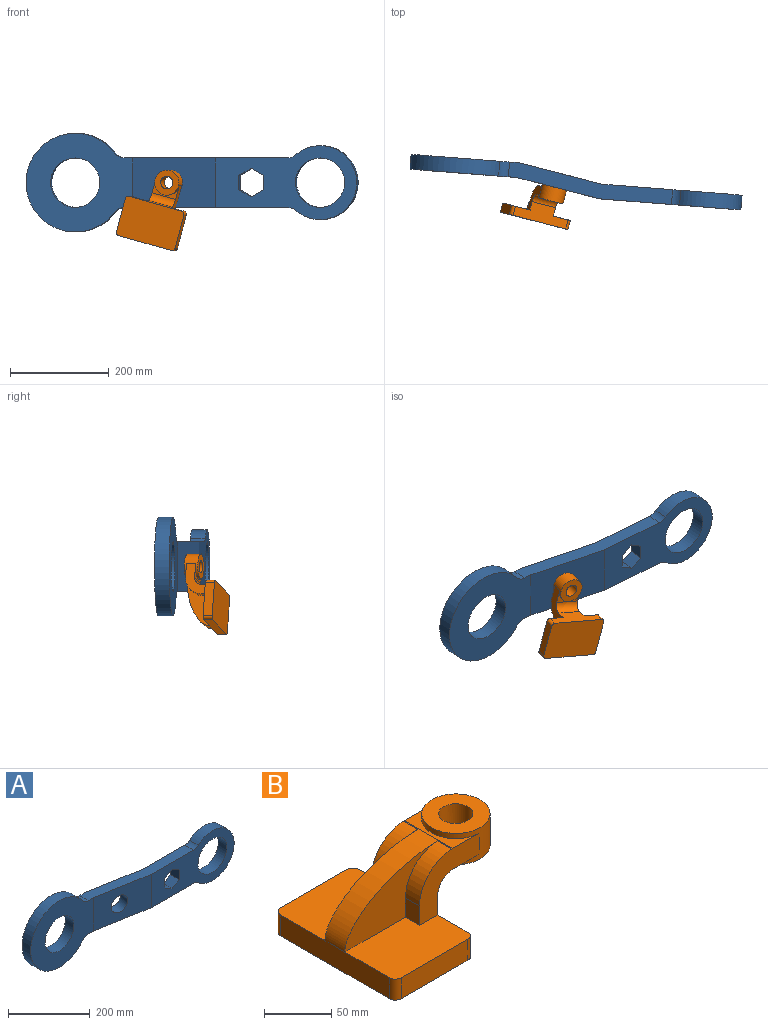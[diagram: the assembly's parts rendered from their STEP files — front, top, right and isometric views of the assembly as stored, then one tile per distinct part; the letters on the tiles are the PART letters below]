
ASSEMBLY  parts=2 mates=1
PART A: 23 faces, bbox 675x60x200 mm
  f0: plane 284.86x150mm, normal (0,1,0), area 21762.9mm2, adj f2,f3,f6,f7,f8,f14,f15,f17
  f1: plane 287.49x150mm, normal (0,-1,0), area 22025.4mm2, adj f2,f4,f6,f7,f8,f14,f15,f17
  f2: cylinder r=50mm len=100mm, axis (0,1,0), area 9424.8mm2, adj f0,f1
  f3: plane 170.14x100mm, normal (0.17,0.98,0), area 15312.8mm2, adj f0,f6,f8,f11,f16
  f4: plane 170.14x100mm, normal (-0.17,-0.98,0), area 15312.8mm2, adj f1,f5,f6,f8,f16
  f5: plane 217.38x200mm, normal (0,-1,0), area 25784.9mm2, adj f4,f6,f8,f9,f10,f12,f13
  f6: plane 333.86x60mm, normal (0,0,-1), area 10094.4mm2, adj f0,f1,f3,f4,f5,f11,f13,f14
  f7: cylinder r=75mm len=150mm, axis (0,1,0), area 10320.9mm2, adj f0,f1,f14,f15
  f8: plane 333.86x60mm, normal (0,0,1), area 10094.4mm2, adj f0,f1,f3,f4,f5,f11,f12,f15
  f9: cylinder r=100mm len=200mm, axis (0,1,0), area 14988.5mm2, adj f5,f11,f12,f13
  f10: cylinder r=50mm len=100mm, axis (0,1,0), area 9424.8mm2, adj f5,f11
  f11: plane 220x200mm, normal (0,1,0), area 26047.4mm2, adj f3,f6,f8,f9,f10,f12,f13
  f12: cylinder r=25mm len=30mm, axis (0,1,0), area 695.5mm2, adj f5,f8,f9,f11
  f13: cylinder r=25mm len=30mm, axis (0,1,0), area 695.5mm2, adj f5,f6,f9,f11
  f14: cylinder r=25mm len=30mm, axis (0,1,0), area 542.1mm2, adj f0,f1,f6,f7
  f15: cylinder r=25mm len=30mm, axis (0,1,0), area 542.1mm2, adj f0,f1,f7,f8
  f16: cylinder r=25mm len=54.45mm, axis (-0.17,-0.98,0), area 4712.4mm2, adj f3,f4
  f17: plane 30x25mm, normal (-0.5,0,-0.87), area 866mm2, adj f0,f1,f18,f22
  f18: plane 30x25mm, normal (0.5,0,-0.87), area 866mm2, adj f0,f1,f17,f19
  f19: plane 30x28.87mm, normal (1,0,0), area 866mm2, adj f0,f1,f18,f20
  f20: plane 30x25mm, normal (0.5,0,0.87), area 866mm2, adj f0,f1,f19,f21
  f21: plane 30x25mm, normal (-0.5,0,0.87), area 866mm2, adj f0,f1,f20,f22
  f22: plane 30x28.87mm, normal (-1,0,0), area 866mm2, adj f0,f1,f17,f21
PART B: 27 faces, bbox 152.4x127x76.2 mm
  f0: plane 17.48x14.92mm, normal (-1,0,0), area 260.8mm2, adj f1,f2,f16,f18
  f1: plane 82.55x53.02mm, normal (0,0,1), area 4075.4mm2, adj f0,f4,f6,f8,f16,f18,f22,f23
  f2: cylinder r=34.92mm len=34.92mm, axis (0,1,0), area 806.4mm2, adj f0,f11,f16,f18
  f3: plane 82.55x53.02mm, normal (0,0,1), area 4075.4mm2, adj f4,f6,f7,f13,f15,f17,f24,f25
  f4: plane 114.3x19.05mm, normal (-1,0,0), area 2177.4mm2, adj f1,f3,f5,f11,f22,f24
  f5: plane 127x82.55mm, normal (0,0,-1), area 10449.2mm2, adj f4,f6,f7,f8,f22,f23,f24,f25
  f6: plane 114.3x36.53mm, normal (1,0,0), area 3065.2mm2, adj f1,f3,f5,f14,f15,f16,f23,f25
  f7: plane 69.85x19.05mm, normal (0,-1,0), area 1330.6mm2, adj f3,f5,f24,f25
  f8: plane 69.85x19.05mm, normal (0,1,0), area 1330.6mm2, adj f1,f5,f22,f23
  f9: plane 50.8x28.58mm, normal (0,0,-1), area 438.2mm2, adj f14,f15,f16,f19
  f10: plane 50.8x28.58mm, normal (0,0,1), area 438.2mm2, adj f11,f15,f16,f19
  f11: extruded ~98.43x52.4mm, area 2524.3mm2, adj f2,f4,f10,f12,f15,f16,f17,f18
  f12: cylinder r=34.92mm len=34.92mm, axis (0,1,0), area 806.4mm2, adj f11,f13,f15,f17
  f13: plane 17.48x14.92mm, normal (-1,0,0), area 260.8mm2, adj f3,f12,f15,f17
  f14: cylinder r=15.88mm len=50.8mm, axis (0,1,0), area 1266.8mm2, adj f6,f9,f15,f16
  f15: plane 63.5x52.4mm, normal (0,-1,0), area 1637.3mm2, adj f3,f6,f9,f10,f11,f12,f13,f14
  f16: plane 63.5x52.4mm, normal (0,1,0), area 1637.3mm2, adj f0,f1,f2,f6,f9,f10,f11,f14
  f17: plane 98.45x52.4mm, normal (0,-1,0), area 2323.5mm2, adj f3,f11,f12,f13
  f18: plane 98.45x52.4mm, normal (0,1,0), area 2323.5mm2, adj f0,f1,f2,f11
  f19: cylinder r=25.4mm len=50.8mm, axis (0,0,-1), area 3040.2mm2, adj f9,f10,f15,f16,f20,f21
  f20: plane 50.8x50.8mm, normal (0,0,-1), area 1520.1mm2, adj f19,f26
  f21: plane 50.8x50.8mm, normal (0,0,1), area 1520.1mm2, adj f19,f26
  f22: cylinder r=6.35mm len=19.05mm, axis (0,0,-1), area 190mm2, adj f1,f4,f5,f8
  f23: cylinder r=6.35mm len=19.05mm, axis (0,0,1), area 190mm2, adj f1,f5,f6,f8
  f24: cylinder r=6.35mm len=19.05mm, axis (0,0,1), area 190mm2, adj f3,f4,f5,f7
  f25: cylinder r=6.35mm len=19.05mm, axis (0,0,-1), area 190mm2, adj f3,f5,f6,f7
  f26: cylinder r=12.7mm len=28.58mm, axis (0,0,1), area 2280.2mm2, adj f20,f21
PLACE A rot(axis=(0,0,-1),4.5deg) t=(-71.82,232.14,13.44)mm fixed
PLACE B rot(axis=(-0.71,-0.41,-0.57),119.5deg) t=(80.13,114.57,-69.26)mm
MATE revolute B.f19 <-> A.f16  axis (0.25,0.97,0) through (118.67,173.48,13.44)mm
